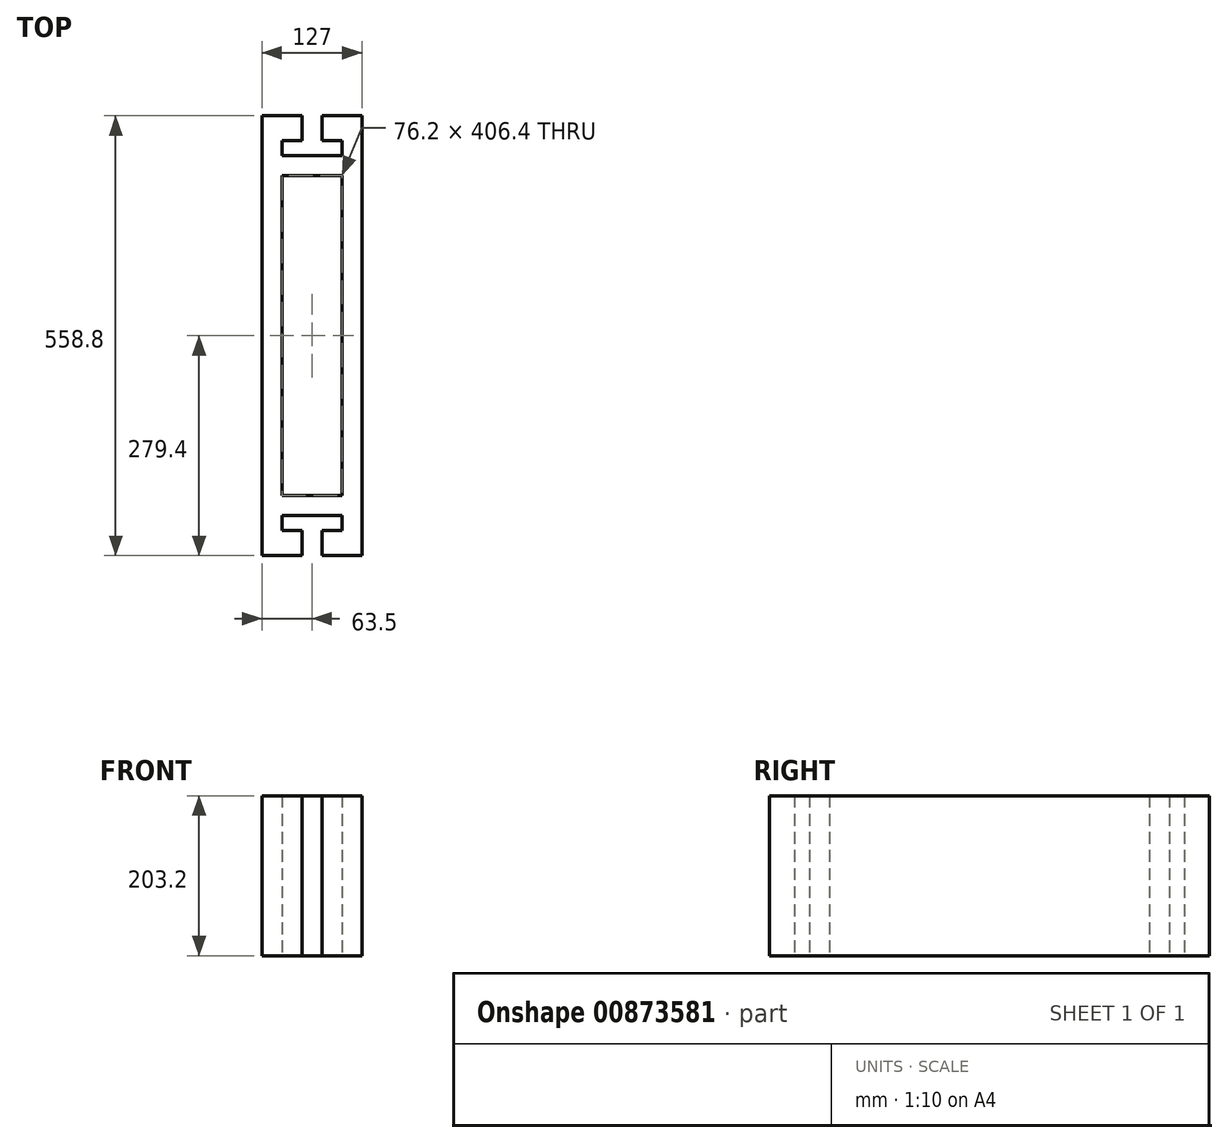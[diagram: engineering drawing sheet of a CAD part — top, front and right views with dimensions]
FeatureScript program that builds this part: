
annotation { "Feature Type Name" : "Feature", "Feature Type Description" : "" }
export const myFeature = defineFeature(function(context is Context, id is Id, definition is map)
    precondition{}
    {
        {
            var Q0;
            Q0=qCreatedBy(makeId("Top.planeOp"),FACE);
            var sketch = newSketch(context, id + "F0", { "sketchPlane" : qUnion([Q0])});
            skLineSegment(sketch, "E0.bottom", {"start": v(0, 0) * mm, "end": v(127, 0) * mm});
            skLineSegment(sketch, "E0.top", {"start": v(0, 457.2) * mm, "end": v(127, 457.2) * mm, "construction": true});
            skLineSegment(sketch, "E0.left", {"start": v(0, 0) * mm, "end": v(0, 457.2) * mm});
            skLineSegment(sketch, "E0.right", {"start": v(127, 0) * mm, "end": v(127, 457.2) * mm});
            skLineSegment(sketch, "E1.0", {"start": v(25.4, 25.4) * mm, "end": v(101.6, 25.4) * mm});
            skLineSegment(sketch, "E1.1", {"start": v(25.4, 25.4) * mm, "end": v(25.4, 431.8) * mm});
            skLineSegment(sketch, "E1.2", {"start": v(25.4, 431.8) * mm, "end": v(101.6, 431.8) * mm});
            skLineSegment(sketch, "E1.3", {"start": v(101.6, 25.4) * mm, "end": v(101.6, 431.8) * mm});
            skLineSegment(sketch, "E2.top", {"start": v(0, 508) * mm, "end": v(50.8, 508) * mm});
            skLineSegment(sketch, "E2.left", {"start": v(0, 457.2) * mm, "end": v(0, 508) * mm});
            skLineSegment(sketch, "E2.right", {"start": v(127, 457.2) * mm, "end": v(127, 508) * mm});
            skLineSegment(sketch, "E3", {"start": v(63.5, 508) * mm, "end": v(63.5, 527.66) * mm, "construction": true});
            skLineSegment(sketch, "E4.top", {"start": v(63.5, 457.2) * mm, "end": v(76.2, 457.2) * mm});
            skLineSegment(sketch, "E4.right", {"start": v(76.2, 508) * mm, "end": v(76.2, 476.25) * mm});
            skLineSegment(sketch, "E5.bottom", {"start": v(76.2, 457.2) * mm, "end": v(101.6, 457.2) * mm});
            skLineSegment(sketch, "E5.top", {"start": v(76.2, 476.25) * mm, "end": v(101.6, 476.25) * mm});
            skLineSegment(sketch, "E5.right", {"start": v(101.6, 457.2) * mm, "end": v(101.6, 476.25) * mm});
            skPoint(sketch, "E6.orphan", {"position": v(63.5, 457.2) * mm});
            skLineSegment(sketch, "E7.MirrorCS", {"start": v(50.8, 508) * mm, "end": v(50.8, 476.25) * mm});
            skLineSegment(sketch, "E8.MirrorCS", {"start": v(50.8, 476.25) * mm, "end": v(25.4, 476.25) * mm});
            skLineSegment(sketch, "E9.MirrorCS", {"start": v(25.4, 457.2) * mm, "end": v(25.4, 476.25) * mm});
            skLineSegment(sketch, "E10.MirrorCS", {"start": v(50.8, 457.2) * mm, "end": v(25.4, 457.2) * mm});
            skLineSegment(sketch, "E11.MirrorCS", {"start": v(63.5, 457.2) * mm, "end": v(50.8, 457.2) * mm});
            skPoint(sketch, "E12.MirrorCS.end.orphan", {"position": v(50.8, 508) * mm});
            skPoint(sketch, "E12.MirrorCS.start.orphan", {"position": v(63.5, 508) * mm});
            skLineSegment(sketch, "E13.trimOffspring", {"start": v(76.2, 508) * mm, "end": v(127, 508) * mm});
            skLineSegment(sketch, "E14", {"start": v(0, 228.6) * mm, "end": v(209.55, 228.6) * mm, "construction": true});
            skLineSegment(sketch, "E15.MirrorCS", {"start": v(25.4, 0) * mm, "end": v(25.4, -19.05) * mm});
            skLineSegment(sketch, "E16.MirrorCS", {"start": v(50.8, -19.05) * mm, "end": v(25.4, -19.05) * mm});
            skLineSegment(sketch, "E17.MirrorCS", {"start": v(50.8, -50.8) * mm, "end": v(50.8, -19.05) * mm});
            skLineSegment(sketch, "E18.MirrorCS", {"start": v(76.2, -50.8) * mm, "end": v(76.2, -19.05) * mm});
            skLineSegment(sketch, "E19.MirrorCS", {"start": v(76.2, -19.05) * mm, "end": v(101.6, -19.05) * mm});
            skLineSegment(sketch, "E20.MirrorCS", {"start": v(101.6, 0) * mm, "end": v(101.6, -19.05) * mm});
            skLineSegment(sketch, "E21.MirrorCS", {"start": v(0, 0) * mm, "end": v(127, 0) * mm, "construction": true});
            skLineSegment(sketch, "E22.MirrorCS", {"start": v(0, -50.8) * mm, "end": v(50.8, -50.8) * mm});
            skLineSegment(sketch, "E23.MirrorCS", {"start": v(76.2, -50.8) * mm, "end": v(127, -50.8) * mm});
            skLineSegment(sketch, "E24.MirrorCS", {"start": v(0, 0) * mm, "end": v(0, -50.8) * mm});
            skLineSegment(sketch, "E25.MirrorCS", {"start": v(127, 0) * mm, "end": v(127, -50.8) * mm});
            skSolve(sketch);
        }
        {
            var Q0;
            Q0=qSketchRegion(id+"F0",true);
            extrude(context, id + "F1", {"entities" : qUnion([Q0]), "depth" : 203.2 * mm, "offsetDistance" : 25.4 * mm});
        }
    });
